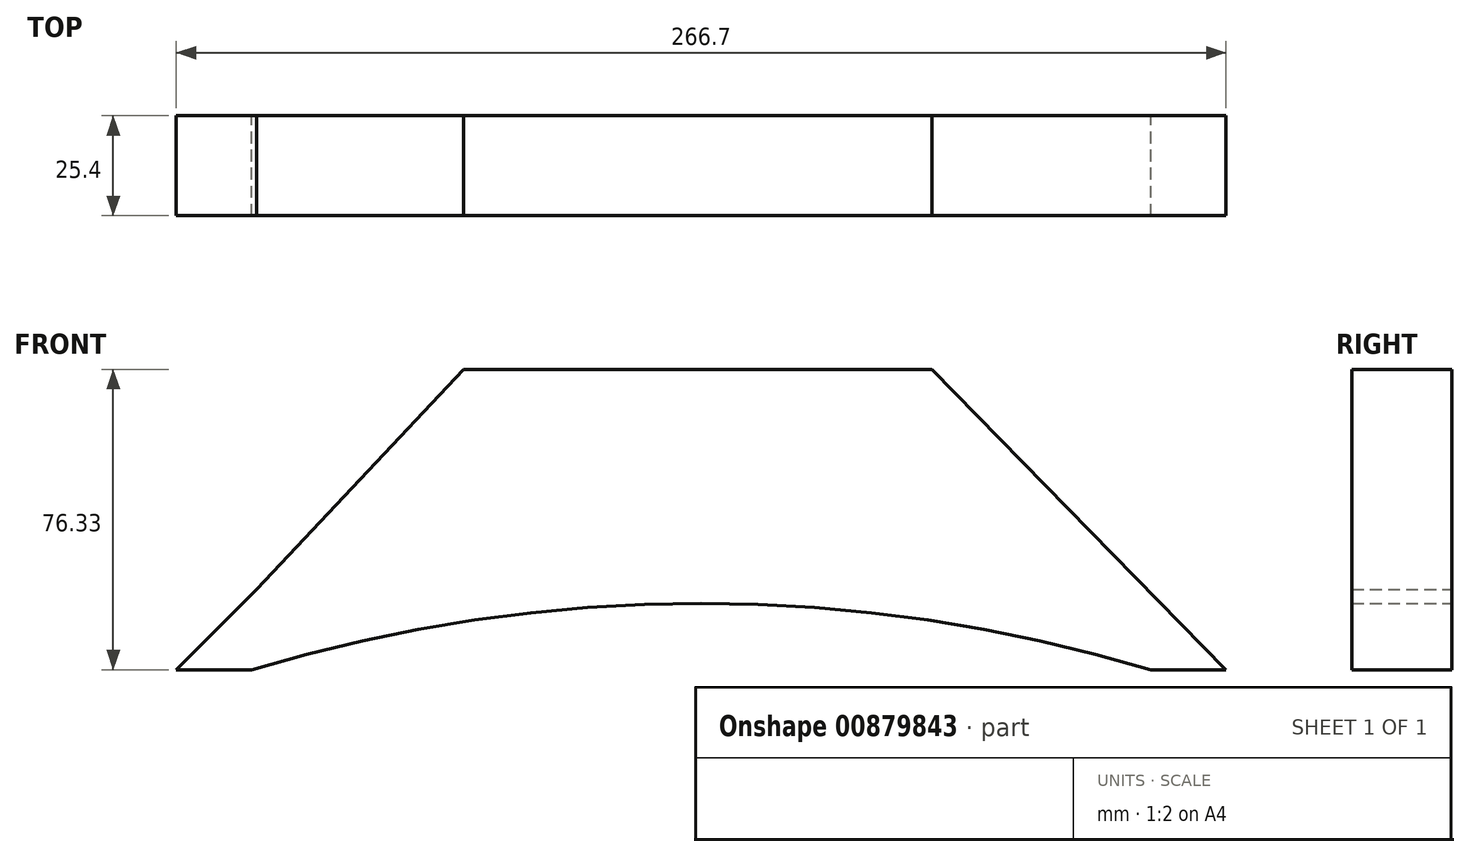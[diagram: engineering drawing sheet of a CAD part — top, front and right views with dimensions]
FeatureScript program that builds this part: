
annotation { "Feature Type Name" : "Feature", "Feature Type Description" : "" }
export const myFeature = defineFeature(function(context is Context, id is Id, definition is map)
    precondition{}
    {
        {
            var Q0;
            Q0=qCreatedBy(makeId("Front.planeOp"),FACE);
            var sketch = newSketch(context, id + "F0", { "sketchPlane" : qUnion([Q0])});
            skLineSegment(sketch, "E0", {"start": v(-121.53, -8.83) * mm, "end": v(-102.39, -8.83) * mm});
            skLineSegment(sketch, "E1", {"start": v(145.17, -8.83) * mm, "end": v(126.03, -8.83) * mm});
            skArc(sketch, "E2", {"start": v(126.03, -8.83) * mm, "mid": v(11.82, 8) * mm, "end": v(-102.39, -8.83) * mm});
            skLineSegment(sketch, "E3", {"start": v(-121.53, -8.83) * mm, "end": v(-101.15, 11.55) * mm});
            skLineSegment(sketch, "E4", {"start": v(-101.15, 11.55) * mm, "end": v(-48.56, 67.5) * mm});
            skLineSegment(sketch, "E5", {"start": v(-48.56, 67.5) * mm, "end": v(70.5, 67.5) * mm});
            skPoint(sketch, "E6.end.orphan", {"position": v(70.5, 65.83) * mm});
            skLineSegment(sketch, "E7", {"start": v(70.5, 67.5) * mm, "end": v(145.17, -8.83) * mm});
            skPoint(sketch, "E8.orphan", {"position": v(11.82, 67.5) * mm});
            skPoint(sketch, "E9.start.orphan", {"position": v(11.82, -8.83) * mm});
            skLineSegment(sketch, "E10.trimOffspring", {"start": v(126.03, -8.83) * mm, "end": v(145.17, -8.83) * mm});
            skSolve(sketch);
        }
        {
            var Q0;
            Q0 = qSketchRegion(id + "F0", true);
            extrude(context, id + "F1", {"entities" : qUnion([Q0]), "depth" : 25.4 * mm, "offsetDistance" : 25.4 * mm});
        }
    });
